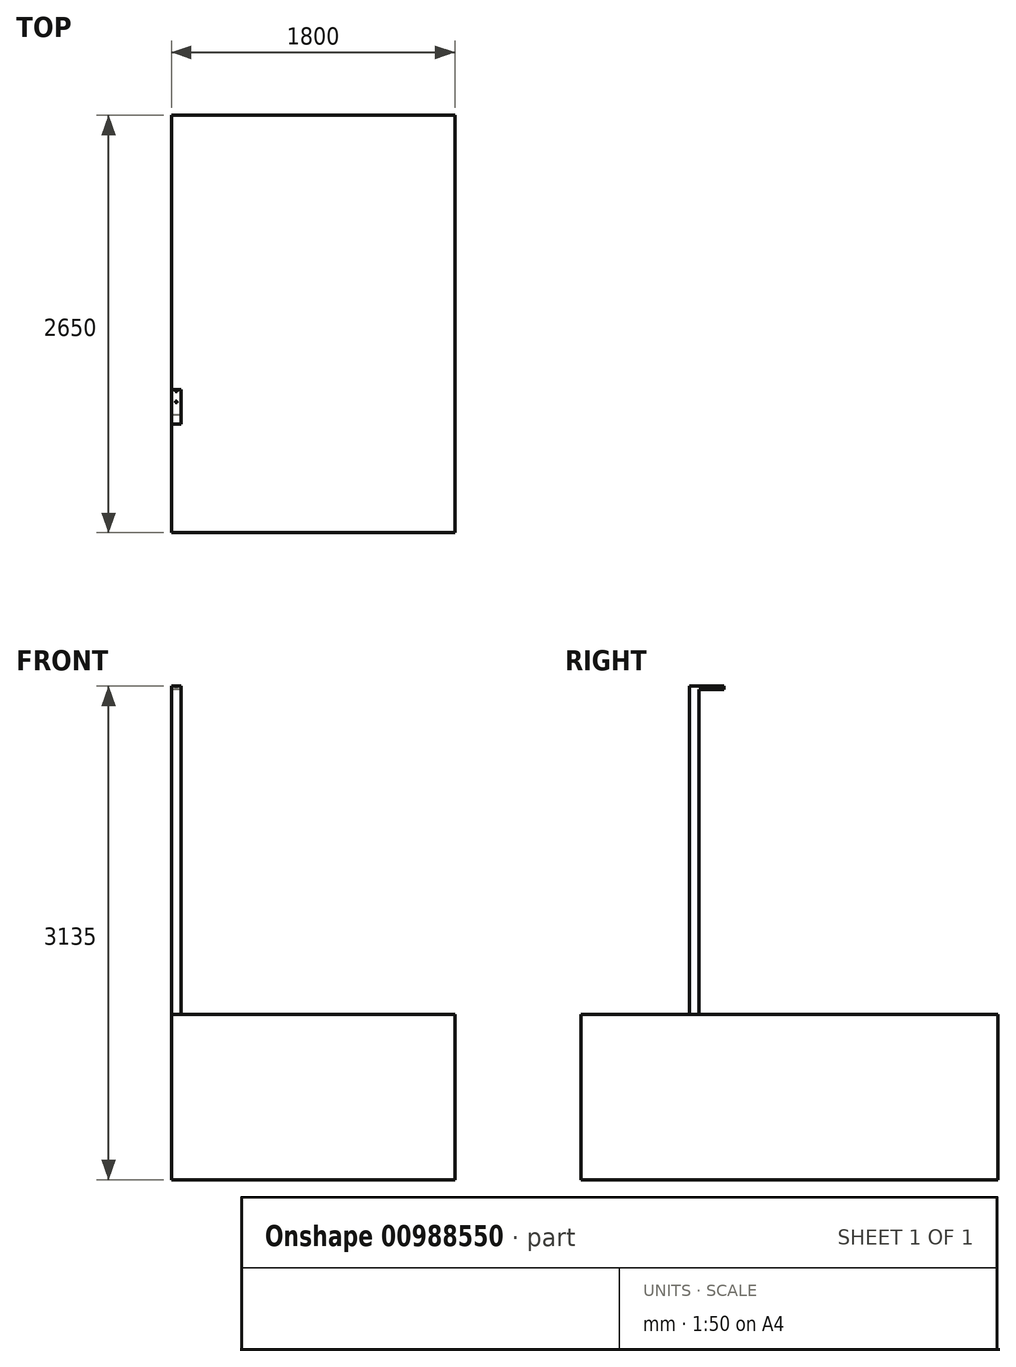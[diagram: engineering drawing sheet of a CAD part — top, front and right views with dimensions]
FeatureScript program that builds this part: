
annotation { "Feature Type Name" : "Feature", "Feature Type Description" : "" }
export const myFeature = defineFeature(function(context is Context, id is Id, definition is map)
    precondition{}
    {
        {
            var Q0;
            Q0=qCreatedBy(makeId("Top.planeOp"),FACE);
            var sketch = newSketch(context, id + "F0", { "sketchPlane" : qUnion([Q0])});
            skLineSegment(sketch, "E0.bottom", {"start": v(-459.8, -1322.36) * mm, "end": v(1340.2, -1322.36) * mm});
            skLineSegment(sketch, "E0.top", {"start": v(-459.8, 1327.64) * mm, "end": v(1340.2, 1327.64) * mm});
            skLineSegment(sketch, "E0.left", {"start": v(-459.8, -1322.36) * mm, "end": v(-459.8, 1327.64) * mm});
            skLineSegment(sketch, "E0.right", {"start": v(1340.2, -1322.36) * mm, "end": v(1340.2, 1327.64) * mm});
            skSolve(sketch);
        }
        {
            var Q0;
            Q0=makeQuery(id+"F0.imprint","IMPRINT",FACE,{"disambiguationData":[TD([[makeQuery(id+"F0.imprint","IMPRINT",EDGE,{"derivedFrom":sQuery(id+"F0.wireOp",EDGE,"E0.bottom")}),1.0]])]});
            extrude(context, id + "F1", {"entities" : qUnion([Q0]), "depth" : 1050 * mm, "offsetDistance" : 25 * mm});
        }
        {
            var Q0;
            Q0=makeQuery(id+"F1.opExtrude","CAP_FACE",FACE,{"disambiguationData":[OSD([sQuery(id+"F0.wireOp",EDGE,"E0.bottom"),sQuery(id+"F0.wireOp",EDGE,"E0.top"),sQuery(id+"F0.wireOp",EDGE,"E0.left"),sQuery(id+"F0.wireOp",EDGE,"E0.right")])],"isStart":false});
            var sketch = newSketch(context, id + "F2", { "sketchPlane" : qUnion([Q0])});
            skLineSegment(sketch, "E1.bottom", {"start": v(-459.8, -632.36) * mm, "end": v(-399.8, -632.36) * mm});
            skLineSegment(sketch, "E1.top", {"start": v(-459.8, -572.36) * mm, "end": v(-399.8, -572.36) * mm});
            skLineSegment(sketch, "E1.left", {"start": v(-459.8, -632.36) * mm, "end": v(-459.8, -572.36) * mm});
            skLineSegment(sketch, "E1.right", {"start": v(-399.8, -632.36) * mm, "end": v(-399.8, -572.36) * mm});
            skSolve(sketch);
        }
        {
            var Q0;
            Q0=makeQuery(id+"F2.imprint","IMPRINT",FACE,{"disambiguationData":[TD([[makeQuery(id+"F2.imprint","IMPRINT",EDGE,{"derivedFrom":sQuery(id+"F2.wireOp",EDGE,"E1.bottom")}),1.0]])]});
            extrude(context, id + "F3", {"entities" : qUnion([Q0]), "operationType" : NewBodyOperationType.ADD, "depth" : 2085 * mm, "offsetDistance" : 25 * mm});
        }
        {
            var Q0;
            Q0=makeQuery(id+"F3.opExtrude","SWEPT_FACE",FACE,{"disambiguationData":[OSD([sQuery(id+"F2.wireOp",EDGE,"E1.top")])]});
            var sketch = newSketch(context, id + "F4", { "sketchPlane" : qUnion([Q0])});
            skLineSegment(sketch, "E2.bottom", {"start": v(399.8, 3135) * mm, "end": v(459.8, 3135) * mm});
            skLineSegment(sketch, "E2.top", {"start": v(399.8, 3115) * mm, "end": v(459.8, 3115) * mm});
            skLineSegment(sketch, "E2.left", {"start": v(399.8, 3135) * mm, "end": v(399.8, 3115) * mm});
            skLineSegment(sketch, "E2.right", {"start": v(459.8, 3135) * mm, "end": v(459.8, 3115) * mm});
            skSolve(sketch);
        }
        {
            var Q0;
            Q0=makeQuery(id+"F4.imprint","IMPRINT",FACE,{"disambiguationData":[TD([[makeQuery(id+"F4.imprint","IMPRINT",EDGE,{"derivedFrom":sQuery(id+"F4.wireOp",EDGE,"E2.bottom")}),1.0]])]});
            extrude(context, id + "F5", {"entities" : qUnion([Q0]), "operationType" : NewBodyOperationType.ADD, "depth" : 160 * mm, "offsetDistance" : 25 * mm});
        }
        {
            var Q0;
            Q0=makeQuery(id+"F5.boolean.opBoolean","MERGE",FACE,{"derivedFrom":[makeQuery(id+"F3.opExtrude","CAP_FACE",FACE,{"disambiguationData":[OSD([sQuery(id+"F2.wireOp",EDGE,"E1.bottom"),sQuery(id+"F2.wireOp",EDGE,"E1.top"),sQuery(id+"F2.wireOp",EDGE,"E1.left"),sQuery(id+"F2.wireOp",EDGE,"E1.right")])],"isStart":false}),makeQuery(id+"F5.opExtrude","SWEPT_FACE",FACE,{"disambiguationData":[OSD([sQuery(id+"F4.wireOp",EDGE,"E2.bottom")])]})]});
            var sketch = newSketch(context, id + "F6", { "sketchPlane" : qUnion([Q0])});
            skCircle(sketch, "E3", {"center": v(-429.8, -422.36) * mm, "radius": 5.24 * mm});
            skCircle(sketch, "E4", {"center": v(-429.8, -492.36) * mm, "radius": 5.2 * mm});
            skSolve(sketch);
        }
        {
            var Q0;
            Q0=makeQuery(id+"F6.imprint","IMPRINT",FACE,{"disambiguationData":[TD([[makeQuery(id+"F6.imprint","IMPRINT",EDGE,{"derivedFrom":sQuery(id+"F6.wireOp",EDGE,"E4")}),1.0]])]});
            var Q1;
            Q1=makeQuery(id+"F6.imprint","IMPRINT",FACE,{"disambiguationData":[TD([[makeQuery(id+"F6.imprint","IMPRINT",EDGE,{"derivedFrom":sQuery(id+"F6.wireOp",EDGE,"E3")}),1.0]])]});
            extrude(context, id + "F7", {"entities" : qUnion([Q0, Q1]), "operationType" : NewBodyOperationType.REMOVE, "endBound" : BoundingType.UP_TO_NEXT, "oppositeDirection" : true, "depth" : 25 * mm, "offsetDistance" : 25 * mm});
        }
    });
